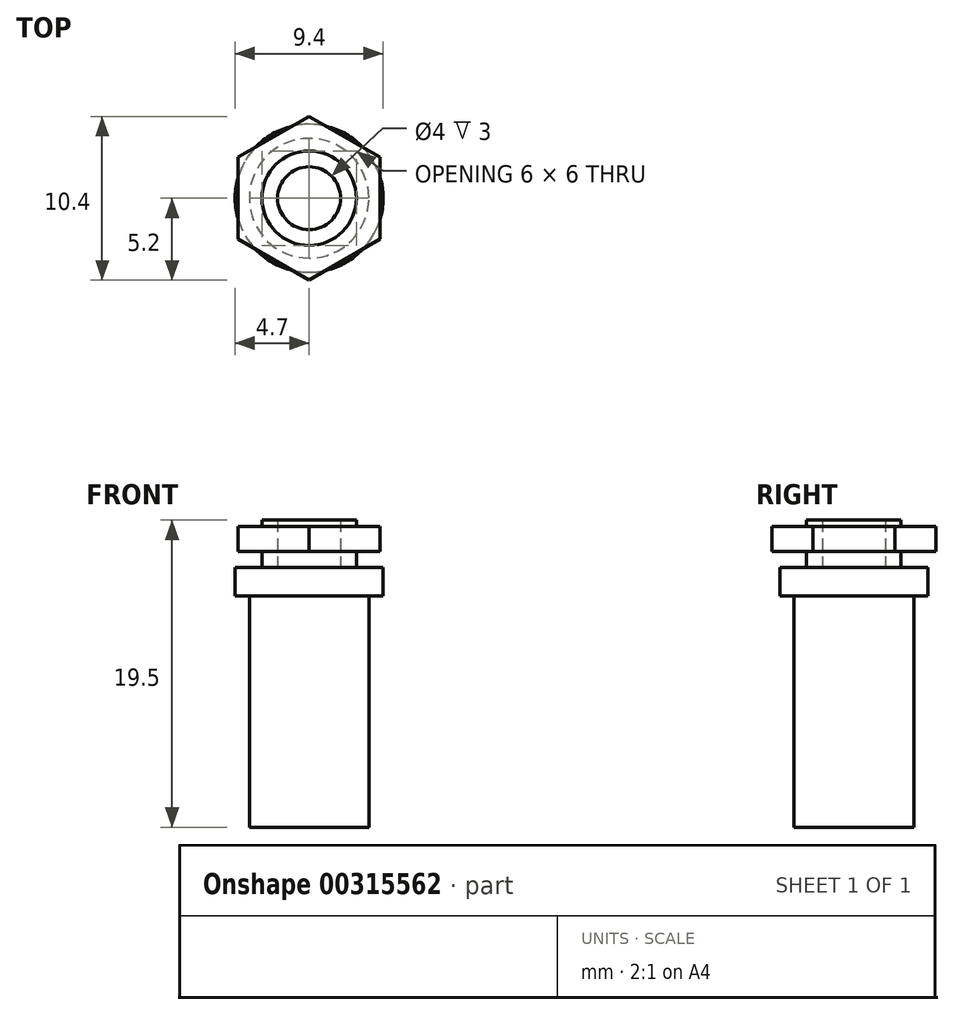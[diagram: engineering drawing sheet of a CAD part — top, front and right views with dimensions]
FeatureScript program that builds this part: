
annotation { "Feature Type Name" : "Feature", "Feature Type Description" : "" }
export const myFeature = defineFeature(function(context is Context, id is Id, definition is map)
    precondition{}
    {
        {
            var Q0;
            Q0=qCreatedBy(makeId("Front.planeOp"),FACE);
            var sketch = newSketch(context, id + "F0", { "sketchPlane" : qUnion([Q0])});
            skLineSegment(sketch, "E0", {"start": v(0, 0) * mm, "end": v(2, 0) * mm});
            skLineSegment(sketch, "E1", {"start": v(2, 0) * mm, "end": v(2, 3) * mm});
            skLineSegment(sketch, "E2", {"start": v(2, 3) * mm, "end": v(3, 3) * mm});
            skLineSegment(sketch, "E3", {"start": v(3, 3) * mm, "end": v(3, 0) * mm});
            skLineSegment(sketch, "E4", {"start": v(3, 0) * mm, "end": v(4.7, 0) * mm});
            skLineSegment(sketch, "E5", {"start": v(4.7, 0) * mm, "end": v(4.7, -1.8) * mm});
            skLineSegment(sketch, "E6", {"start": v(4.7, -1.8) * mm, "end": v(3.8, -1.8) * mm});
            skLineSegment(sketch, "E7", {"start": v(3.8, -1.8) * mm, "end": v(3.8, -16.5) * mm});
            skLineSegment(sketch, "E8", {"start": v(3.8, -16.5) * mm, "end": v(0, -16.5) * mm});
            skLineSegment(sketch, "E9", {"start": v(0, -16.5) * mm, "end": v(0, 0) * mm});
            skSolve(sketch);
        }
        {
            var Q0;
            Q0 = qSketchRegion(id + "F0", true);
            var Q1;
            Q1=sQuery(id+"F0.wireOp",EDGE,"E9");
            revolve(context, id + "F1", {"entities" : qUnion([Q0]), "axis" : qUnion([Q1]), "revolveType" : RevolveType.FULL});
        }
        {
            var Q0;
            Q0=makeQuery(id+"F1.opRevolve","SWEPT_FACE",FACE,{"disambiguationData":[OSD([sQuery(id+"F0.wireOp",EDGE,"E4")])]});
            cPlane(context, id + "F2", {"entities" : qUnion([Q0]), "cplaneType" : CPlaneType.OFFSET, "offset" : 1 * mm, "width" : 150 * mm, "height" : 150 * mm});
        }
        {
            var Q0;
            Q0=qCreatedBy(id+"F2.planeOp",FACE);
            var sketch = newSketch(context, id + "F3", { "sketchPlane" : qUnion([Q0])});
            skCircle(sketch, "E10.cCircle", {"center": v(0, 0) * mm, "radius": 4.5 * mm, "construction": true});
            skLineSegment(sketch, "E10.0", {"start": v(4.5, 2.6) * mm, "end": v(4.5, -2.6) * mm});
            skLineSegment(sketch, "E10.1", {"start": v(4.5, -2.6) * mm, "end": v(0, -5.2) * mm});
            skLineSegment(sketch, "E10.2", {"start": v(0, -5.2) * mm, "end": v(-4.5, -2.6) * mm});
            skLineSegment(sketch, "E10.3", {"start": v(-4.5, -2.6) * mm, "end": v(-4.5, 2.6) * mm});
            skLineSegment(sketch, "E10.4", {"start": v(-4.5, 2.6) * mm, "end": v(0, 5.2) * mm});
            skLineSegment(sketch, "E10.5", {"start": v(0, 5.2) * mm, "end": v(4.5, 2.6) * mm});
            skPoint(sketch, "E10.0.midPoint", {"position": v(4.5, 0) * mm});
            skCircle(sketch, "E11.0", {"center": v(0, 0) * mm, "radius": 2 * mm});
            skSolve(sketch);
        }
        {
            var Q0;
            Q0 = qSketchRegion(id + "F3", true);
            extrude(context, id + "F4", {"entities" : qUnion([Q0]), "operationType" : NewBodyOperationType.ADD, "depth" : 1.6 * mm});
        }
    });
